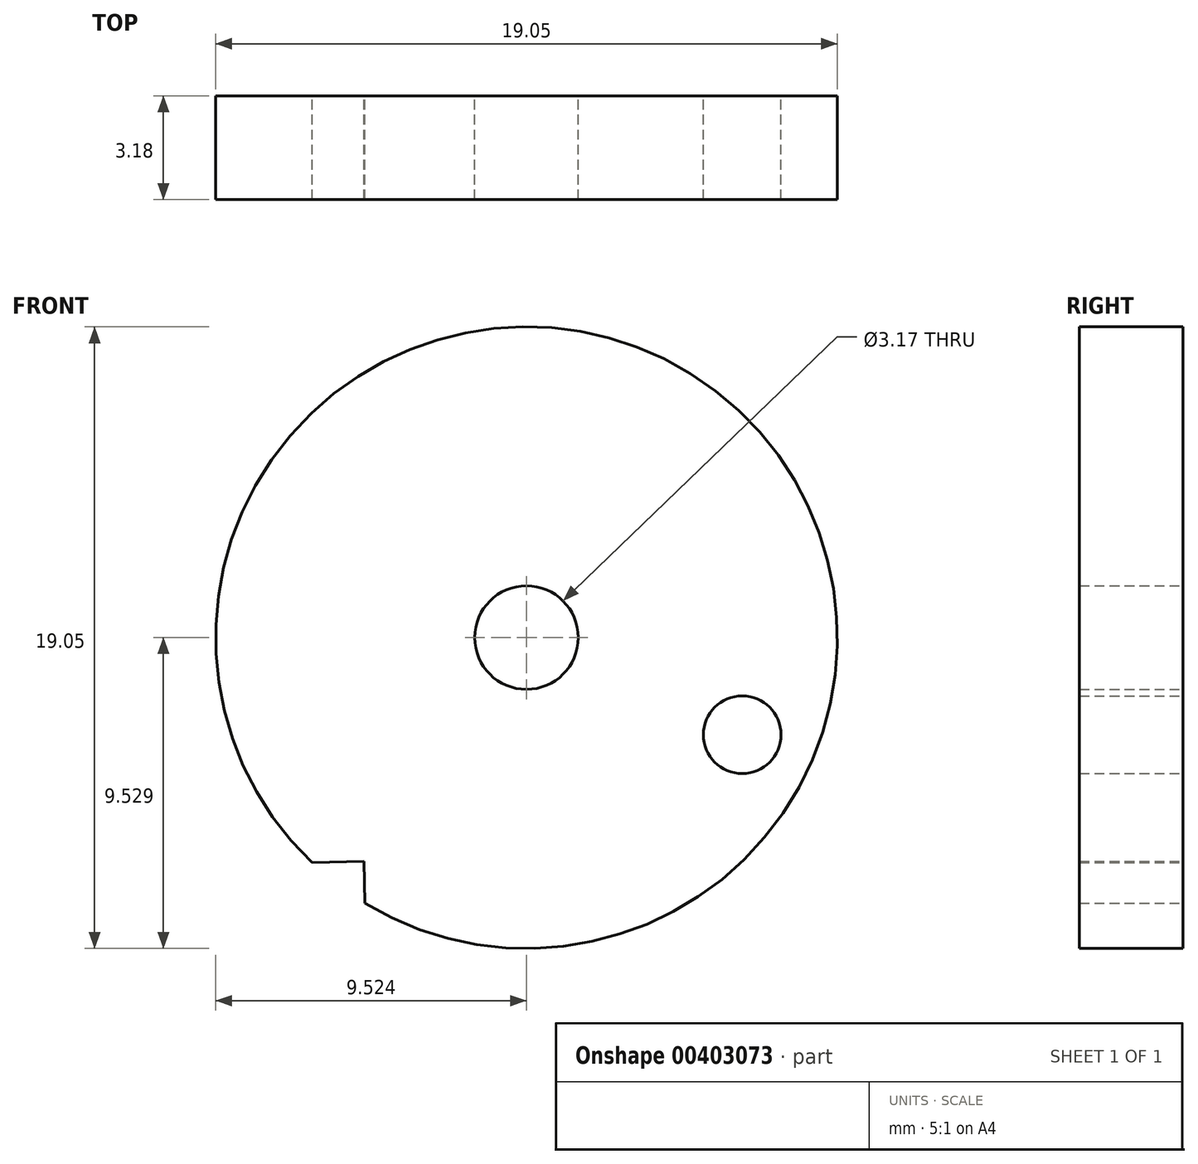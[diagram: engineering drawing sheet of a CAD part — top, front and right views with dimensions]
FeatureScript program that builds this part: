
annotation { "Feature Type Name" : "Feature", "Feature Type Description" : "" }
export const myFeature = defineFeature(function(context is Context, id is Id, definition is map)
    precondition{}
    {
        {
            var Q0;
            Q0=qCreatedBy(makeId("Front.planeOp"),FACE);
            var sketch = newSketch(context, id + "F0", { "sketchPlane" : qUnion([Q0])});
            skArc(sketch, "E0", {"start": v(-4.16, -4.72) * mm, "mid": v(6.58, 10.98) * mm, "end": v(-5.78, -3.48) * mm});
            skCircle(sketch, "E1", {"center": v(0.78, 3.42) * mm, "radius": 1.59 * mm});
            skLineSegment(sketch, "E2", {"start": v(-5.78, -3.48) * mm, "end": v(-4.2, -3.44) * mm});
            skLineSegment(sketch, "E3", {"start": v(-4.2, -3.44) * mm, "end": v(-4.16, -4.72) * mm});
            skCircle(sketch, "E4", {"center": v(7.4, 0.44) * mm, "radius": 1.2 * mm});
            skSolve(sketch);
        }
        {
            var Q0;
            Q0=makeQuery(id+"F0.imprint","IMPRINT",FACE,{"disambiguationData":[TD([[makeQuery(id+"F0.imprint","IMPRINT",EDGE,{"derivedFrom":sQuery(id+"F0.wireOp",EDGE,"E0")}),1.0]])]});
            extrude(context, id + "F1", {"entities" : qUnion([Q0]), "endBound" : BoundingType.SYMMETRIC, "depth" : 3.17 * mm});
        }
    });
